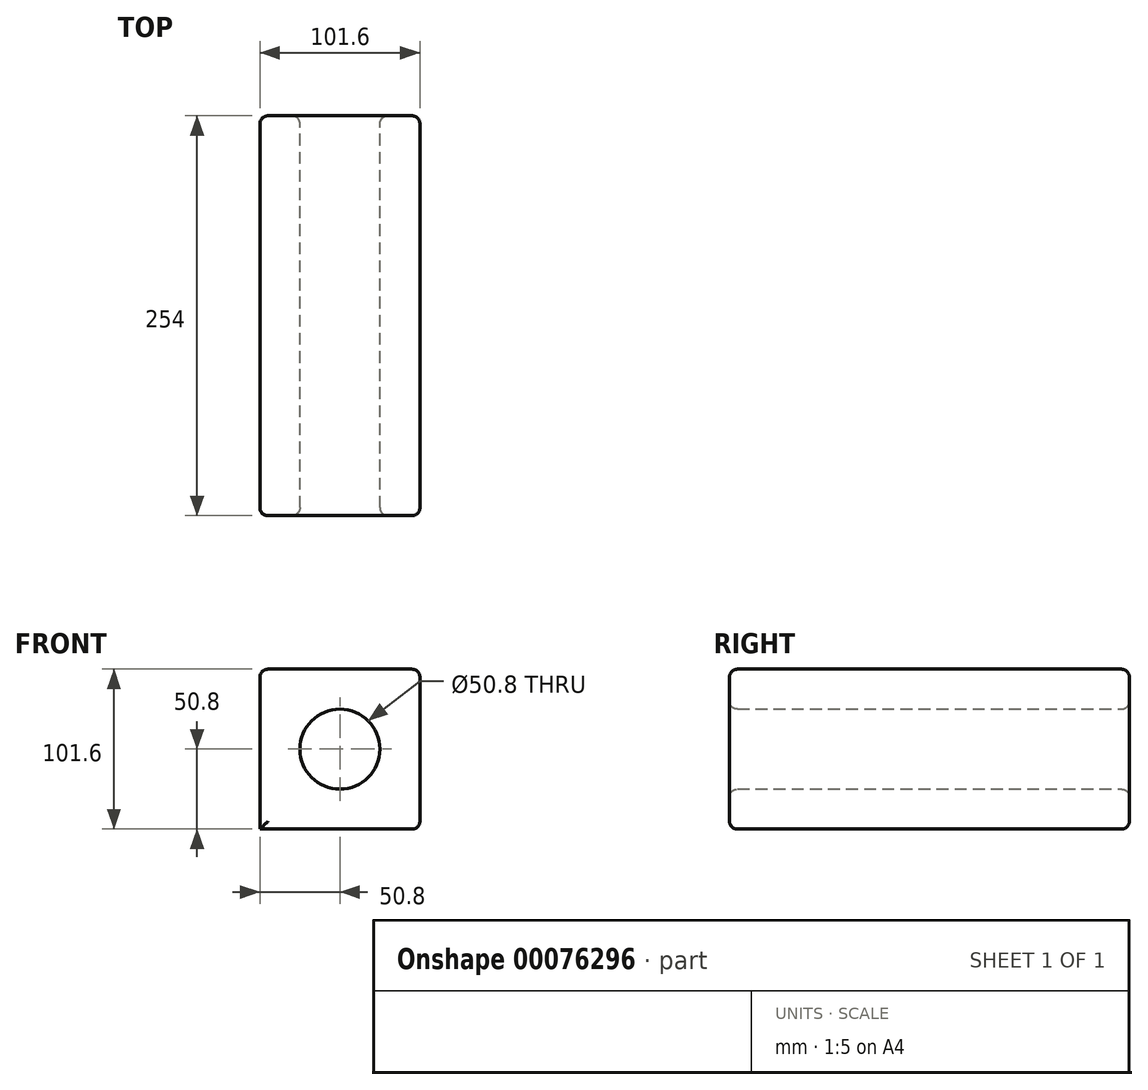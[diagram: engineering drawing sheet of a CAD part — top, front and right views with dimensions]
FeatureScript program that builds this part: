
annotation { "Feature Type Name" : "Feature", "Feature Type Description" : "" }
export const myFeature = defineFeature(function(context is Context, id is Id, definition is map)
    precondition{}
    {
        {
            var Q0;
            Q0=qCreatedBy(makeId("Front.planeOp"),FACE);
            var sketch = newSketch(context, id + "F0", { "sketchPlane" : qUnion([Q0])});
            skCircle(sketch, "E0", {"center": v(0, 0) * mm, "radius": 25.4 * mm});
            skLineSegment(sketch, "E1.bottom", {"start": v(-50.8, 50.8) * mm, "end": v(50.8, 50.8) * mm});
            skLineSegment(sketch, "E1.top", {"start": v(-50.8, -50.8) * mm, "end": v(50.8, -50.8) * mm});
            skLineSegment(sketch, "E1.left", {"start": v(-50.8, 50.8) * mm, "end": v(-50.8, -50.8) * mm});
            skLineSegment(sketch, "E1.right", {"start": v(50.8, 50.8) * mm, "end": v(50.8, -50.8) * mm});
            skSolve(sketch);
        }
        {
            var Q0;
            Q0 = qSketchRegion(id + "F0", true);
            extrude(context, id + "F1", {"entities" : qUnion([Q0]), "depth" : 254 * mm});
        }
        {
            var Q0;
            Q0=makeQuery(id+"F1.opExtrude","CAP_EDGE",EDGE,{"disambiguationData":[OSD([sQuery(id+"F0.wireOp",EDGE,"E1.bottom")])],"isStart":false});
            var Q1;
            Q1=makeQuery(id+"F1.opExtrude","SWEPT_EDGE",EDGE,{"disambiguationData":[OSD([sQuery(id+"F0.wireOp",EDGE,"E1.bottom"),sQuery(id+"F0.wireOp",EDGE,"E1.right")])]});
            var Q2;
            Q2=makeQuery(id+"F1.opExtrude","SWEPT_EDGE",EDGE,{"disambiguationData":[OSD([sQuery(id+"F0.wireOp",EDGE,"E1.bottom"),sQuery(id+"F0.wireOp",EDGE,"E1.left")])]});
            var Q3;
            Q3=makeQuery(id+"F1.opExtrude","CAP_EDGE",EDGE,{"disambiguationData":[OSD([sQuery(id+"F0.wireOp",EDGE,"E1.bottom")])],"isStart":true});
            var Q4;
            Q4=makeQuery(id+"F1.opExtrude","CAP_EDGE",EDGE,{"disambiguationData":[OSD([sQuery(id+"F0.wireOp",EDGE,"E1.right")])],"isStart":false});
            var Q5;
            Q5=makeQuery(id+"F1.opExtrude","CAP_FACE",FACE,{"disambiguationData":[OSD([sQuery(id+"F0.wireOp",EDGE,"E0"),sQuery(id+"F0.wireOp",EDGE,"E1.bottom"),sQuery(id+"F0.wireOp",EDGE,"E1.top"),sQuery(id+"F0.wireOp",EDGE,"E1.left"),sQuery(id+"F0.wireOp",EDGE,"E1.right")])],"isStart":false});
            var Q6;
            Q6=makeQuery(id+"F1.opExtrude","CAP_EDGE",EDGE,{"disambiguationData":[OSD([sQuery(id+"F0.wireOp",EDGE,"E1.top")])],"isStart":false});
            var Q7;
            Q7=makeQuery(id+"F1.opExtrude","SWEPT_EDGE",EDGE,{"disambiguationData":[OSD([sQuery(id+"F0.wireOp",EDGE,"E1.top"),sQuery(id+"F0.wireOp",EDGE,"E1.right")])]});
            var Q8;
            Q8=makeQuery(id+"F1.opExtrude","CAP_EDGE",EDGE,{"disambiguationData":[OSD([sQuery(id+"F0.wireOp",EDGE,"E1.right")])],"isStart":true});
            var Q9;
            Q9=makeQuery(id+"F1.opExtrude","CAP_EDGE",EDGE,{"disambiguationData":[OSD([sQuery(id+"F0.wireOp",EDGE,"E1.left")])],"isStart":false});
            var Q10;
            Q10=makeQuery(id+"F1.opExtrude","CAP_EDGE",EDGE,{"disambiguationData":[OSD([sQuery(id+"F0.wireOp",EDGE,"E1.left")])],"isStart":true});
            var Q11;
            Q11=makeQuery(id+"F1.opExtrude","CAP_EDGE",EDGE,{"disambiguationData":[OSD([sQuery(id+"F0.wireOp",EDGE,"E1.top")])],"isStart":true});
            var Q12;
            Q12=makeQuery(id+"F1.opExtrude","CAP_EDGE",EDGE,{"disambiguationData":[OSD([sQuery(id+"F0.wireOp",EDGE,"E0")])],"isStart":true});
            fillet(context, id + "F2", {"entities" : qUnion([Q0, Q1, Q2, Q3, Q4, Q5, Q6, Q7, Q8, Q9, Q10, Q11, Q12]), "radius" : 5.08 * mm, "tangentPropagation" : true, "allowEdgeOverflow" : false});
        }
    });
